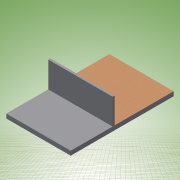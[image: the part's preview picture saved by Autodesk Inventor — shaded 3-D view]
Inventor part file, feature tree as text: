
AUTODESK INVENTOR PART (.ipt)
format: ipt  version: 2017 (Build 210142000, 142)  size: 118,272 bytes
history: native  units: mm
features: extrude x2, sketch x2
ambient origin geometry x8: Origin, YZ Plane, XZ Plane, XY Plane, X Axis, Y Axis, Z Axis, Center Point
bodies: Solid1 (feature_tree)
feature tree (4):
  extrude  "Extrusion1"  Depth=101.6mm TaperAngle=0.0deg
  extrude  "Extrusion2"  Depth=2438.4mm
  sketch  "Sketch1"  dims[d0=1524.0mm d1=101.6mm d2=0.0mm]
  sketch  "Sketch2"  dims[d3=609.6mm d4=0.0mm d5=2438.4mm d6=50.8mm d7=1524.0mm d8=0.0mm]
